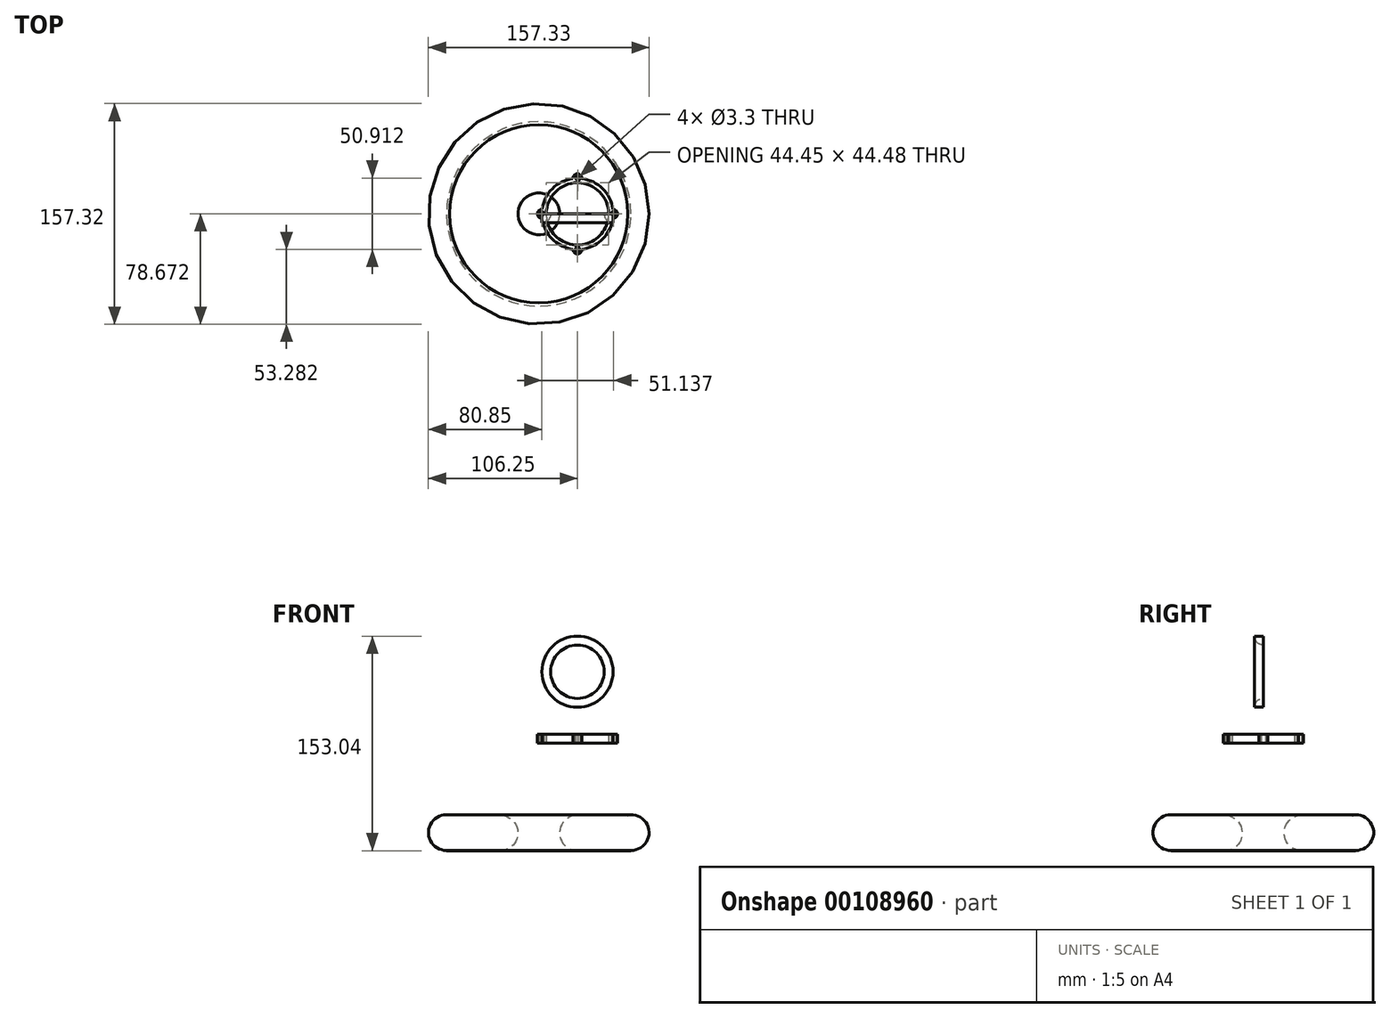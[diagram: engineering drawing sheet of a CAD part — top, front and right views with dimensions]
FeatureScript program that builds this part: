
annotation { "Feature Type Name" : "Feature", "Feature Type Description" : "" }
export const myFeature = defineFeature(function(context is Context, id is Id, definition is map)
    precondition{}
    {
        {
            var Q0;
            Q0=qCreatedBy(makeId("Top.planeOp"),FACE);
            var sketch = newSketch(context, id + "F0", { "sketchPlane" : qUnion([Q0])});
            skCircle(sketch, "E0", {"center": v(0, 0) * mm, "radius": 25.4 * mm});
            skCircle(sketch, "E1", {"center": v(0, 25.4) * mm, "radius": 3.18 * mm});
            skCircle(sketch, "E2", {"center": v(-25.4, 0) * mm, "radius": 3.18 * mm});
            skCircle(sketch, "E3", {"center": v(25.4, 0) * mm, "radius": 3.18 * mm});
            skCircle(sketch, "E4", {"center": v(0, -25.4) * mm, "radius": 3.18 * mm});
            skCircle(sketch, "E5", {"center": v(0, 0) * mm, "radius": 22.23 * mm});
            skCircle(sketch, "E6", {"center": v(-25.4, 0) * mm, "radius": 1.65 * mm});
            skCircle(sketch, "E7", {"center": v(0.1, -25.38) * mm, "radius": 1.65 * mm});
            skCircle(sketch, "E8", {"center": v(25.74, 0.11) * mm, "radius": 1.65 * mm});
            skCircle(sketch, "E9", {"center": v(0.42, 25.53) * mm, "radius": 1.65 * mm});
            skLineSegment(sketch, "E10", {"start": v(0.42, 25.53) * mm, "end": v(0.1, -25.38) * mm});
            skSolve(sketch);
        }
        {
            var Q0;
            Q0=qCreatedBy(makeId("Right.planeOp"),FACE);
            var sketch = newSketch(context, id + "F1", { "sketchPlane" : qUnion([Q0])});
            skCircle(sketch, "E11", {"center": v(0, 76.2) * mm, "radius": 12.7 * mm});
            skLineSegment(sketch, "E12.bottom", {"start": v(-12.7, 76.17) * mm, "end": v(12.7, 76.17) * mm});
            skLineSegment(sketch, "E12.top", {"start": v(-12.7, 76.19) * mm, "end": v(12.7, 76.19) * mm});
            skLineSegment(sketch, "E12.left", {"start": v(-12.7, 76.17) * mm, "end": v(-12.7, 76.19) * mm});
            skLineSegment(sketch, "E12.right", {"start": v(12.7, 76.17) * mm, "end": v(12.7, 76.19) * mm});
            skLineSegment(sketch, "E13.top", {"start": v(-12.7, 50.8) * mm, "end": v(12.7, 50.8) * mm});
            skLineSegment(sketch, "E13.left", {"start": v(-12.7, 76.19) * mm, "end": v(-12.7, 50.8) * mm});
            skLineSegment(sketch, "E13.right", {"start": v(12.7, 76.19) * mm, "end": v(12.7, 50.8) * mm});
            skCircle(sketch, "E14", {"center": v(0, 76.2) * mm, "radius": 6.35 * mm});
            skLineSegment(sketch, "E15", {"start": v(0, 76.2) * mm, "end": v(0, 50.8) * mm});
            skLineSegment(sketch, "E16", {"start": v(12.7, 76.19) * mm, "end": v(0, 50.8) * mm});
            skLineSegment(sketch, "E17", {"start": v(-12.7, 76.19) * mm, "end": v(0, 50.8) * mm});
            skSolve(sketch);
        }
        {
            var Q0;
            Q0 = qSketchRegion(id + "F0", true);
            extrude(context, id + "F2", {"entities" : qUnion([Q0]), "depth" : 6.35 * mm});
        }
        {
            var Q0;
            {var subQ0=sQuery(id+"F1.wireOp",EDGE,"E14");var subQ1=sQuery(id+"F1.wireOp",EDGE,"E12.top");var subQ2=makeQuery(id+"F1.imprint","INTERSECT",VERTEX,{"disambiguationData":[OD(0.0)],"derivedFrom":[subQ1,subQ0]});Q0=makeQuery(id+"F1.imprint","IMPRINT",FACE,{"disambiguationData":[TD([[makeQuery(id+"F1.imprint","IMPRINT",EDGE,{"disambiguationData":[TD([[subQ2,-1.0]])],"derivedFrom":subQ1}),1.0]])]});}
            var Q1;
            {var subQ0=sQuery(id+"F1.wireOp",EDGE,"E14");var subQ1=sQuery(id+"F1.wireOp",EDGE,"E12.bottom");var subQ2=makeQuery(id+"F1.imprint","INTERSECT",VERTEX,{"disambiguationData":[OD(0.0)],"derivedFrom":[subQ1,subQ0]});Q1=makeQuery(id+"F1.imprint","IMPRINT",FACE,{"disambiguationData":[TD([[makeQuery(id+"F1.imprint","IMPRINT",EDGE,{"disambiguationData":[TD([[subQ2,-1.0]])],"derivedFrom":subQ1}),-1.0]])]});}
            var Q2;
            {var subQ0=sQuery(id+"F1.wireOp",EDGE,"E13.left");var subQ3=sQuery(id+"F1.wireOp",EDGE,"E12.top");var subQ4=makeQuery(id+"F1.imprint","INTERSECT",VERTEX,{"derivedFrom":[subQ3,subQ0]});Q2=makeQuery(id+"F1.imprint","IMPRINT",FACE,{"disambiguationData":[TD([[makeQuery(id+"F1.imprint","IMPRINT",EDGE,{"disambiguationData":[TD([[subQ4,-1.0]])],"derivedFrom":subQ3}),1.0]])]});}
            var Q3;
            Q3=sQuery(id+"F1.wireOp",EDGE,"E13.top");
            revolve(context, id + "F3", {"entities" : qUnion([Q0, Q1, Q2]), "axis" : qUnion([Q3]), "revolveType" : RevolveType.FULL});
        }
        {
            var Q0;
            Q0=qCreatedBy(makeId("Front.planeOp"),FACE);
            var sketch = newSketch(context, id + "F4", { "sketchPlane" : qUnion([Q0])});
            skCircle(sketch, "E18", {"center": v(0, -64.17) * mm, "radius": 12.7 * mm});
            skLineSegment(sketch, "E19.bottom", {"start": v(-27.59, -50.25) * mm, "end": v(-65.69, -50.25) * mm});
            skLineSegment(sketch, "E19.top", {"start": v(-27.59, -75.65) * mm, "end": v(-65.69, -75.65) * mm});
            skLineSegment(sketch, "E19.left", {"start": v(-27.59, -50.25) * mm, "end": v(-27.59, -75.65) * mm});
            skLineSegment(sketch, "E19.right", {"start": v(-65.69, -50.25) * mm, "end": v(-65.69, -75.65) * mm});
            skLineSegment(sketch, "E20.bottom", {"start": v(0, -51.47) * mm, "end": v(38.1, -51.47) * mm});
            skLineSegment(sketch, "E20.top", {"start": v(0, -76.87) * mm, "end": v(38.1, -76.87) * mm});
            skLineSegment(sketch, "E20.left", {"start": v(0, -51.47) * mm, "end": v(0, -76.87) * mm});
            skLineSegment(sketch, "E20.right", {"start": v(38.1, -51.47) * mm, "end": v(38.1, -76.87) * mm});
            skCircle(sketch, "E21", {"center": v(38.38, -63.93) * mm, "radius": 12.7 * mm});
            skSolve(sketch);
        }
        {
            var Q0;
            {var subQ0=sQuery(id+"F4.wireOp",EDGE,"E20.left");Q0=makeQuery(id+"F4.imprint","IMPRINT",FACE,{"disambiguationData":[TD([[makeQuery(id+"F4.imprint","IMPRINT",EDGE,{"derivedFrom":subQ0}),1.0]])]});}
            var Q1;
            {var subQ0=sQuery(id+"F4.wireOp",EDGE,"E20.left");Q1=makeQuery(id+"F4.imprint","IMPRINT",FACE,{"disambiguationData":[TD([[makeQuery(id+"F4.imprint","IMPRINT",EDGE,{"derivedFrom":subQ0}),-1.0]])]});}
            var Q2;
            {var subQ1=sQuery(id+"F4.wireOp",EDGE,"E20.bottom");Q2=makeQuery(id+"F4.imprint","IMPRINT",FACE,{"disambiguationData":[TD([[makeQuery(id+"F4.imprint","IMPRINT",EDGE,{"derivedFrom":subQ1}),-1.0]])]});}
            var Q3;
            {var subQ0=sQuery(id+"F4.wireOp",EDGE,"E20.top");Q3=makeQuery(id+"F4.imprint","IMPRINT",FACE,{"disambiguationData":[TD([[makeQuery(id+"F4.imprint","IMPRINT",EDGE,{"derivedFrom":subQ0}),1.0]])]});}
            var Q4;
            {var subQ0=sQuery(id+"F4.wireOp",EDGE,"E20.right");var subQ1=sQuery(id+"F4.wireOp",EDGE,"E20.bottom");var subQ2=makeQuery(id+"F4.imprint","INTERSECT",VERTEX,{"derivedFrom":[subQ1,subQ0]});Q4=makeQuery(id+"F4.imprint","IMPRINT",FACE,{"disambiguationData":[TD([[makeQuery(id+"F4.imprint","IMPRINT",EDGE,{"disambiguationData":[TD([[subQ2,1.0]])],"derivedFrom":subQ1}),1.0]])]});}
            var Q5;
            Q5=sQuery(id+"F4.wireOp",EDGE,"E19.left");
            revolve(context, id + "F5", {"entities" : qUnion([Q0, Q1, Q2, Q3, Q4]), "axis" : qUnion([Q5]), "revolveType" : RevolveType.FULL});
        }
    });
